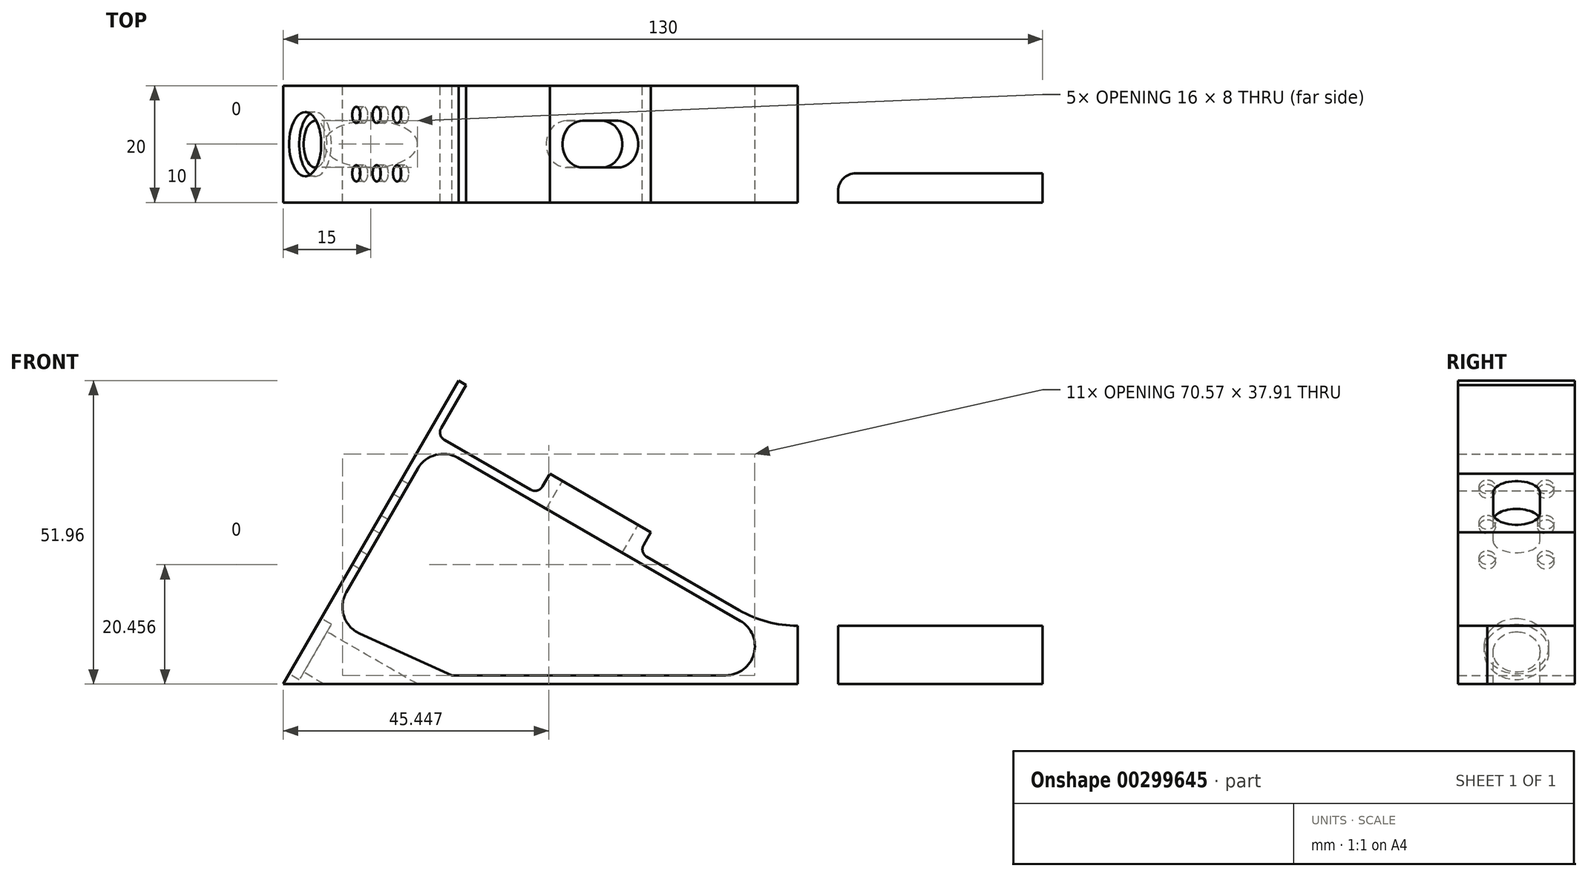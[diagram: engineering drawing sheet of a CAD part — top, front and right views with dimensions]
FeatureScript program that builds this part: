
annotation { "Feature Type Name" : "Feature", "Feature Type Description" : "" }
export const myFeature = defineFeature(function(context is Context, id is Id, definition is map)
    precondition{}
    {
        {
            var Q0;
            Q0=qCreatedBy(makeId("Front.planeOp"),FACE);
            var sketch = newSketch(context, id + "F0", { "sketchPlane" : qUnion([Q0])});
            skLineSegment(sketch, "E0", {"start": v(0, 0) * mm, "end": v(130, 0) * mm});
            skLineSegment(sketch, "E1", {"start": v(0, 0) * mm, "end": v(30, 51.96) * mm});
            skLineSegment(sketch, "E2", {"start": v(30, 51.96) * mm, "end": v(31.3, 51.21) * mm});
            skLineSegment(sketch, "E3", {"start": v(130, 10) * mm, "end": v(130, 0) * mm});
            skLineSegment(sketch, "E4", {"start": v(31.3, 51.21) * mm, "end": v(27.05, 43.85) * mm});
            skLineSegment(sketch, "E5", {"start": v(27.6, 41.8) * mm, "end": v(42.32, 33.3) * mm});
            skLineSegment(sketch, "E6", {"start": v(44.37, 33.85) * mm, "end": v(45.62, 36.02) * mm});
            skLineSegment(sketch, "E7", {"start": v(45.62, 36.02) * mm, "end": v(62.94, 26.02) * mm});
            skLineSegment(sketch, "E8", {"start": v(62.94, 26.02) * mm, "end": v(61.7, 23.85) * mm});
            skPoint(sketch, "E9.visualSharp", {"position": v(26.3, 42.55) * mm});
            skArc(sketch, "E9.filletArc", {"start": v(27.05, 43.85) * mm, "mid": v(26.9, 42.71) * mm, "end": v(27.6, 41.8) * mm});
            skPoint(sketch, "E10.visualSharp", {"position": v(43.62, 32.55) * mm});
            skArc(sketch, "E10.filletArc", {"start": v(42.32, 33.3) * mm, "mid": v(43.46, 33.15) * mm, "end": v(44.37, 33.85) * mm});
            skLineSegment(sketch, "E11", {"start": v(62.24, 21.8) * mm, "end": v(78.04, 12.68) * mm});
            skLineSegment(sketch, "E12", {"start": v(88.04, 10) * mm, "end": v(130, 10) * mm});
            skPoint(sketch, "E13.visualSharp", {"position": v(60.94, 22.55) * mm});
            skArc(sketch, "E13.filletArc", {"start": v(61.7, 23.85) * mm, "mid": v(61.54, 22.71) * mm, "end": v(62.24, 21.8) * mm});
            skPoint(sketch, "E14.visualSharp", {"position": v(82.68, 10) * mm});
            skArc(sketch, "E14.filletArc", {"start": v(78.04, 12.68) * mm, "mid": v(82.86, 10.68) * mm, "end": v(88.04, 10) * mm});
            skLineSegment(sketch, "E15", {"start": v(10.8, 15.72) * mm, "end": v(23.05, 36.92) * mm});
            skLineSegment(sketch, "E16", {"start": v(29.88, 38.75) * mm, "end": v(78.24, 10.83) * mm});
            skLineSegment(sketch, "E17", {"start": v(75.74, 1.5) * mm, "end": v(28.86, 1.5) * mm});
            skPoint(sketch, "E18.visualSharp", {"position": v(25.55, 41.25) * mm});
            skArc(sketch, "E18.filletArc", {"start": v(29.88, 38.75) * mm, "mid": v(26.09, 39.25) * mm, "end": v(23.05, 36.92) * mm});
            skPoint(sketch, "E19.visualSharp", {"position": v(94.4, 1.5) * mm});
            skArc(sketch, "E19.filletArc", {"start": v(75.74, 1.5) * mm, "mid": v(80.57, 5.2) * mm, "end": v(78.24, 10.83) * mm});
            skLineSegment(sketch, "E20", {"start": v(13.07, 8.66) * mm, "end": v(28.86, 1.5) * mm});
            skPoint(sketch, "E21.visualSharp", {"position": v(8.05, 10.94) * mm});
            skArc(sketch, "E21.filletArc", {"start": v(10.8, 15.72) * mm, "mid": v(10.38, 11.69) * mm, "end": v(13.07, 8.66) * mm});
            skSolve(sketch);
        }
        {
            var Q0;
            Q0 = qSketchRegion(id + "F0", true);
            extrude(context, id + "F1", {"entities" : qUnion([Q0]), "depth" : 20 * mm});
        }
        {
            var Q0;
            Q0=makeQuery(id+"F1.opExtrude","SWEPT_FACE",FACE,{"disambiguationData":[OSD([sQuery(id+"F0.wireOp",EDGE,"E1")])]});
            var sketch = newSketch(context, id + "F2", { "sketchPlane" : qUnion([Q0])});
            skCircle(sketch, "E22", {"center": v(10, 7.5) * mm, "radius": 5.5 * mm});
            skPoint(sketch, "E22.centerSnap0", {"position": v(10, 0) * mm});
            skCircle(sketch, "E23", {"center": v(10, 7.5) * mm, "radius": 4 * mm});
            skCircle(sketch, "E24", {"center": v(5, 25) * mm, "radius": 1.4 * mm});
            skCircle(sketch, "E25", {"center": v(15, 25) * mm, "radius": 1.4 * mm});
            skCircle(sketch, "E26", {"center": v(15, 32) * mm, "radius": 1.4 * mm});
            skCircle(sketch, "E27", {"center": v(15, 39) * mm, "radius": 1.4 * mm});
            skCircle(sketch, "E28", {"center": v(5, 39) * mm, "radius": 1.4 * mm});
            skCircle(sketch, "E29", {"center": v(5, 32) * mm, "radius": 1.4 * mm});
            skSolve(sketch);
        }
        {
            var Q0;
            Q0 = qSketchRegion(id + "F2", true);
            extrude(context, id + "F3", {"entities" : qUnion([Q0]), "operationType" : NewBodyOperationType.REMOVE, "oppositeDirection" : true, "depth" : 2 * mm});
        }
        {
            var Q0;
            Q0=makeQuery(id+"F3.boolean.opBoolean","SPLIT",FACE,{"disambiguationData":[TD([makeQuery(id+"F3.opExtrude","SWEPT_FACE",FACE,{"disambiguationData":[OSD([sQuery(id+"F2.wireOp",EDGE,"E23")])]})])],"derivedFrom":makeQuery(id+"F1.opExtrude","SWEPT_FACE",FACE,{"disambiguationData":[OSD([sQuery(id+"F0.wireOp",EDGE,"E1")])]})});
            extrude(context, id + "F4", {"entities" : qUnion([Q0]), "operationType" : NewBodyOperationType.REMOVE, "endBound" : BoundingType.THROUGH_ALL, "oppositeDirection" : true, "depth" : 25 * mm});
        }
        {
            var Q0;
            Q0=makeQuery(id+"F1.opExtrude","SWEPT_FACE",FACE,{"disambiguationData":[OSD([sQuery(id+"F0.wireOp",EDGE,"E12")])]});
            var sketch = newSketch(context, id + "F5", { "sketchPlane" : qUnion([Q0])});
            skLineSegment(sketch, "E30", {"start": v(130, -10) * mm, "end": v(60.97, -10) * mm, "construction": true});
            skPoint(sketch, "E30.endSnap0", {"position": v(130, -10) * mm});
            skLineSegment(sketch, "E31.0", {"start": v(130, -10) * mm, "end": v(130, -7) * mm});
            skLineSegment(sketch, "E32", {"start": v(130, -7) * mm, "end": v(113, -7) * mm});
            skArc(sketch, "E33", {"start": v(113, -7) * mm, "mid": v(110.88, -7.88) * mm, "end": v(110, -10) * mm});
            skLineSegment(sketch, "E34", {"start": v(130, -5) * mm, "end": v(98, -5) * mm});
            skLineSegment(sketch, "E35", {"start": v(95, -2) * mm, "end": v(95, 0) * mm});
            skLineSegment(sketch, "E36.trimOffspring", {"start": v(130, -5) * mm, "end": v(130, 0) * mm});
            skPoint(sketch, "E37.orphan", {"position": v(130, -20) * mm});
            skPoint(sketch, "E38.visualSharp", {"position": v(95, -5) * mm});
            skArc(sketch, "E38.filletArc", {"start": v(95, -2) * mm, "mid": v(95.88, -4.12) * mm, "end": v(98, -5) * mm});
            skLineSegment(sketch, "E39.MirrorCS", {"start": v(130, -10) * mm, "end": v(130, -13) * mm});
            skArc(sketch, "E40.MirrorCS", {"start": v(95, -18) * mm, "mid": v(95.88, -15.88) * mm, "end": v(98, -15) * mm});
            skLineSegment(sketch, "E41.MirrorCS", {"start": v(95, -18) * mm, "end": v(95, -20) * mm});
            skPoint(sketch, "E42.MirrorP", {"position": v(130, 0) * mm});
            skLineSegment(sketch, "E43.MirrorCS", {"start": v(130, -13) * mm, "end": v(113, -13) * mm});
            skPoint(sketch, "E44.MirrorP", {"position": v(95, -15) * mm});
            skLineSegment(sketch, "E45.MirrorCS", {"start": v(130, -15) * mm, "end": v(130, -20) * mm});
            skLineSegment(sketch, "E46.MirrorCS", {"start": v(130, -15) * mm, "end": v(98, -15) * mm});
            skArc(sketch, "E47.MirrorCS", {"start": v(113, -13) * mm, "mid": v(110.88, -12.12) * mm, "end": v(110, -10) * mm});
            skSolve(sketch);
        }
        {
            var Q0;
            Q0 = qSketchRegion(id + "F5", true);
            var Q1;
            Q1=makeQuery(id+"F5.imprint","IMPRINT",FACE,{"disambiguationData":[TD([[makeQuery(id+"F5.imprint","IMPRINT",EDGE,{"derivedFrom":sQuery(id+"F5.wireOp",EDGE,"E40.MirrorCS")}),-1.0]])]});
            var Q2;
            Q2=makeQuery(id+"F5.imprint","IMPRINT",FACE,{"disambiguationData":[TD([[makeQuery(id+"F5.imprint","IMPRINT",EDGE,{"derivedFrom":sQuery(id+"F5.wireOp",EDGE,"E34")}),-1.0]])]});
            extrude(context, id + "F6", {"entities" : qUnion([Q0, Q1, Q2]), "operationType" : NewBodyOperationType.REMOVE, "endBound" : BoundingType.THROUGH_ALL, "oppositeDirection" : true, "depth" : 25 * mm});
        }
        {
            var Q0;
            Q0=makeQuery(id+"F1.opExtrude","SWEPT_FACE",FACE,{"disambiguationData":[OSD([sQuery(id+"F0.wireOp",EDGE,"E7")])]});
            var sketch = newSketch(context, id + "F7", { "sketchPlane" : qUnion([Q0])});
            skLineSegment(sketch, "E48", {"start": v(21.5, -10) * mm, "end": v(41.5, -10) * mm, "construction": true});
            skArc(sketch, "E49", {"start": v(28, -6) * mm, "mid": v(25.17, -7.17) * mm, "end": v(24, -10) * mm});
            skLineSegment(sketch, "E50", {"start": v(28, -6) * mm, "end": v(35, -6) * mm});
            skArc(sketch, "E51", {"start": v(39, -10) * mm, "mid": v(37.83, -7.17) * mm, "end": v(35, -6) * mm});
            skArc(sketch, "E52.MirrorCS", {"start": v(28, -14) * mm, "mid": v(25.17, -12.83) * mm, "end": v(24, -10) * mm});
            skLineSegment(sketch, "E53.MirrorCS", {"start": v(28, -14) * mm, "end": v(35, -14) * mm});
            skArc(sketch, "E54.MirrorCS", {"start": v(39, -10) * mm, "mid": v(37.83, -12.83) * mm, "end": v(35, -14) * mm});
            skSolve(sketch);
        }
        {
            var Q0;
            Q0 = qSketchRegion(id + "F7", true);
            extrude(context, id + "F8", {"entities" : qUnion([Q0]), "operationType" : NewBodyOperationType.REMOVE, "endBound" : BoundingType.UP_TO_NEXT, "oppositeDirection" : true, "depth" : 25 * mm});
        }
    });
